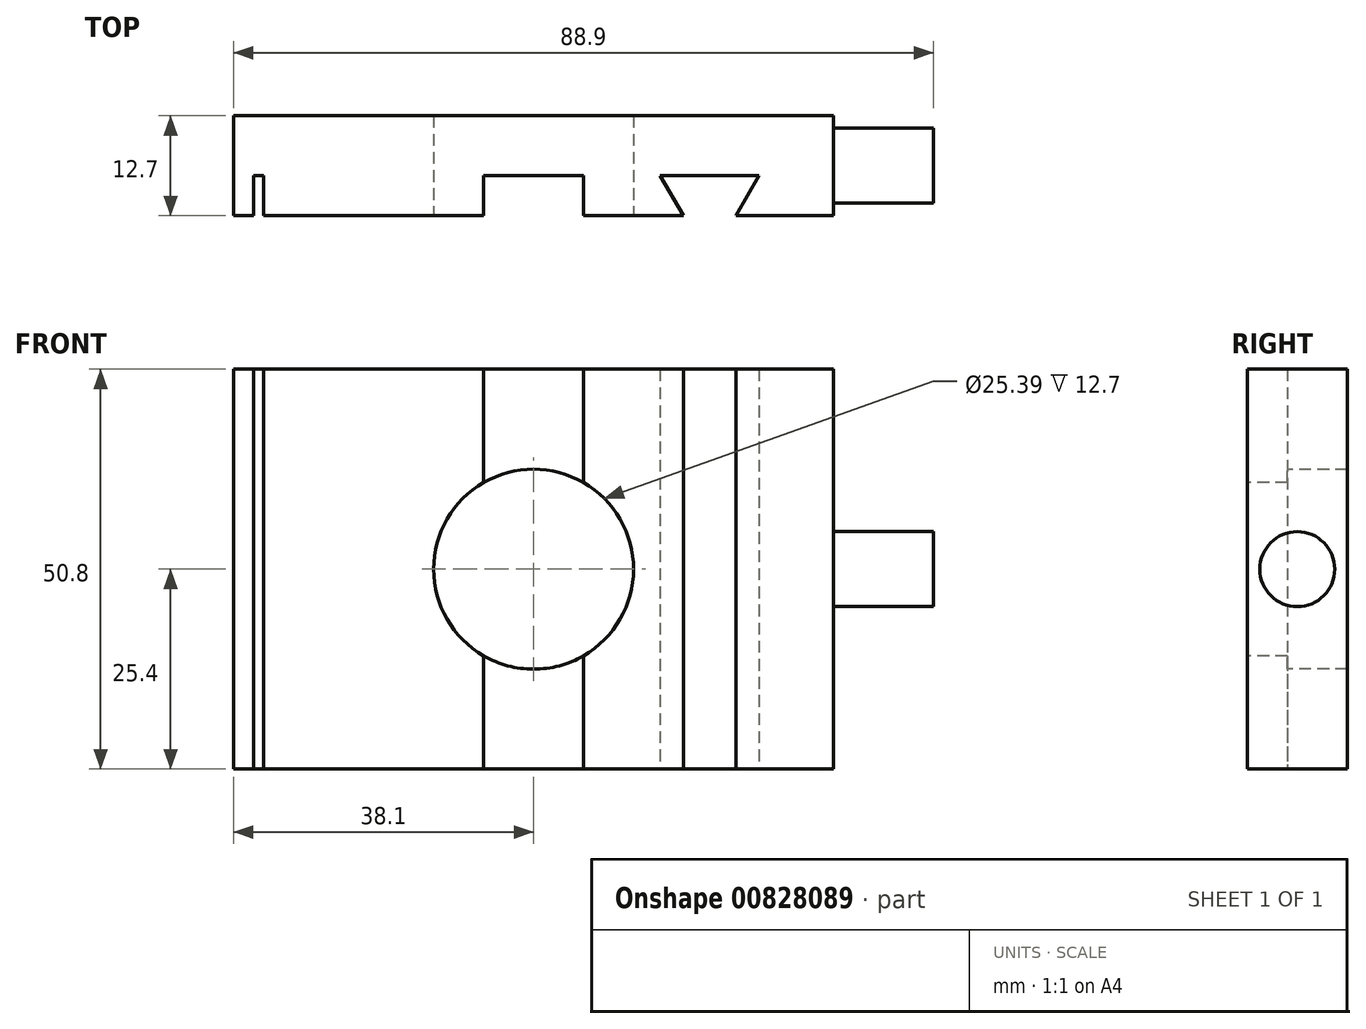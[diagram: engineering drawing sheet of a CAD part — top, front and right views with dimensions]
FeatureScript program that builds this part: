
annotation { "Feature Type Name" : "Feature", "Feature Type Description" : "" }
export const myFeature = defineFeature(function(context is Context, id is Id, definition is map)
    precondition{}
    {
        {
            var Q0;
            Q0=qCreatedBy(makeId("Front.planeOp"),FACE);
            var sketch = newSketch(context, id + "F0", { "sketchPlane" : qUnion([Q0])});
            skLineSegment(sketch, "E0.bottom", {"start": v(38.1, 25.4) * mm, "end": v(-38.1, 25.4) * mm});
            skLineSegment(sketch, "E0.top", {"start": v(38.1, -25.4) * mm, "end": v(-38.1, -25.4) * mm});
            skLineSegment(sketch, "E0.left", {"start": v(38.1, 25.4) * mm, "end": v(38.1, -25.4) * mm});
            skLineSegment(sketch, "E0.right", {"start": v(-38.1, 25.4) * mm, "end": v(-38.1, -25.4) * mm});
            skPoint(sketch, "E0.middle", {"position": v(0, 0) * mm});
            skSolve(sketch);
        }
        {
            var Q0;
            Q0=makeQuery(id+"F0.imprint","IMPRINT",FACE,{"disambiguationData":[TD([[makeQuery(id+"F0.imprint","IMPRINT",EDGE,{"derivedFrom":sQuery(id+"F0.wireOp",EDGE,"E0.bottom")}),1.0]])]});
            extrude(context, id + "F1", {"entities" : qUnion([Q0]), "depth" : 12.7 * mm, "offsetDistance" : 25.4 * mm});
        }
        {
            var Q0;
            Q0=makeQuery(id+"F1.opExtrude","CAP_FACE",FACE,{"disambiguationData":[OSD([sQuery(id+"F0.wireOp",EDGE,"E0.bottom"),sQuery(id+"F0.wireOp",EDGE,"E0.top"),sQuery(id+"F0.wireOp",EDGE,"E0.left"),sQuery(id+"F0.wireOp",EDGE,"E0.right")])],"isStart":false});
            var sketch = newSketch(context, id + "F2", { "sketchPlane" : qUnion([Q0])});
            skLineSegment(sketch, "E1.bottom", {"start": v(-35.56, 25.4) * mm, "end": v(-34.29, 25.4) * mm});
            skLineSegment(sketch, "E1.top", {"start": v(-35.56, -25.4) * mm, "end": v(-34.29, -25.4) * mm});
            skLineSegment(sketch, "E1.left", {"start": v(-35.56, 25.4) * mm, "end": v(-35.56, -25.4) * mm});
            skLineSegment(sketch, "E1.right", {"start": v(-34.29, 25.4) * mm, "end": v(-34.29, -25.4) * mm});
            skCircle(sketch, "E2", {"center": v(0, 0) * mm, "radius": 12.7 * mm});
            skLineSegment(sketch, "E3.bottom", {"start": v(6.35, 25.4) * mm, "end": v(-6.35, 25.4) * mm});
            skLineSegment(sketch, "E3.top", {"start": v(6.35, -25.4) * mm, "end": v(-6.35, -25.4) * mm});
            skLineSegment(sketch, "E3.left", {"start": v(6.35, 25.4) * mm, "end": v(6.35, -25.4) * mm});
            skLineSegment(sketch, "E3.right", {"start": v(-6.35, 25.4) * mm, "end": v(-6.35, -25.4) * mm});
            skSolve(sketch);
        }
        {
            var Q0;
            {var subQ0=sQuery(id+"F2.wireOp",EDGE,"E3.right");var subQ1=sQuery(id+"F2.wireOp",EDGE,"E2");var subQ2=makeQuery(id+"F2.imprint","INTERSECT",VERTEX,{"disambiguationData":[OD(0.0)],"derivedFrom":[subQ1,subQ0]});Q0=makeQuery(id+"F2.imprint","IMPRINT",FACE,{"disambiguationData":[TD([[makeQuery(id+"F2.imprint","IMPRINT",EDGE,{"disambiguationData":[TD([[subQ2,-1.0]])],"derivedFrom":subQ1}),1.0]])]});}
            var Q1;
            {var subQ0=sQuery(id+"F2.wireOp",EDGE,"E3.right");var subQ1=sQuery(id+"F2.wireOp",EDGE,"E2");var subQ2=makeQuery(id+"F2.imprint","INTERSECT",VERTEX,{"disambiguationData":[OD(0.0)],"derivedFrom":[subQ1,subQ0]});Q1=makeQuery(id+"F2.imprint","IMPRINT",FACE,{"disambiguationData":[TD([[makeQuery(id+"F2.imprint","IMPRINT",EDGE,{"disambiguationData":[TD([[subQ2,1.0]])],"derivedFrom":subQ1}),1.0]])]});}
            var Q2;
            {var subQ0=sQuery(id+"F2.wireOp",EDGE,"E3.left");var subQ1=sQuery(id+"F2.wireOp",EDGE,"E2");var subQ2=makeQuery(id+"F2.imprint","INTERSECT",VERTEX,{"disambiguationData":[OD(0.0)],"derivedFrom":[subQ1,subQ0]});Q2=makeQuery(id+"F2.imprint","IMPRINT",FACE,{"disambiguationData":[TD([[makeQuery(id+"F2.imprint","IMPRINT",EDGE,{"disambiguationData":[TD([[subQ2,1.0]])],"derivedFrom":subQ1}),1.0]])]});}
            extrude(context, id + "F3", {"entities" : qUnion([Q0, Q1, Q2]), "operationType" : NewBodyOperationType.REMOVE, "oppositeDirection" : true, "depth" : 12.7 * mm, "offsetDistance" : 25.4 * mm});
        }
        {
            var Q0;
            Q0 = qSketchRegion(id + "F2", true);
            extrude(context, id + "F4", {"entities" : qUnion([Q0]), "operationType" : NewBodyOperationType.REMOVE, "oppositeDirection" : true, "depth" : 5.08 * mm, "offsetDistance" : 25.4 * mm});
        }
        {
            var Q0;
            Q0=makeQuery(id+"F1.opExtrude","SWEPT_FACE",FACE,{"disambiguationData":[OSD([sQuery(id+"F0.wireOp",EDGE,"E0.top")])]});
            var sketch = newSketch(context, id + "F5", { "sketchPlane" : qUnion([Q0])});
            skLineSegment(sketch, "E4", {"start": v(19.02, 12.7) * mm, "end": v(16.09, 7.62) * mm});
            skLineSegment(sketch, "E5", {"start": v(28.64, 7.62) * mm, "end": v(25.7, 12.7) * mm});
            skLineSegment(sketch, "E6", {"start": v(25.7, 12.7) * mm, "end": v(19.02, 12.7) * mm});
            skLineSegment(sketch, "E7", {"start": v(16.09, 7.62) * mm, "end": v(28.64, 7.62) * mm});
            skSolve(sketch);
        }
        {
            var Q0;
            Q0 = qSketchRegion(id + "F5", true);
            extrude(context, id + "F6", {"entities" : qUnion([Q0]), "operationType" : NewBodyOperationType.REMOVE, "oppositeDirection" : true, "depth" : 50.8 * mm, "offsetDistance" : 25.4 * mm});
        }
        {
            var Q0;
            Q0=makeQuery(id+"F1.opExtrude","SWEPT_FACE",FACE,{"disambiguationData":[OSD([sQuery(id+"F0.wireOp",EDGE,"E0.left")])]});
            var sketch = newSketch(context, id + "F7", { "sketchPlane" : qUnion([Q0])});
            skCircle(sketch, "E8", {"center": v(-6.35, 0) * mm, "radius": 4.76 * mm});
            skPoint(sketch, "E8.centerSnap0", {"position": v(-12.7, 0) * mm});
            skPoint(sketch, "E8.centerSnap1", {"position": v(-6.35, -25.4) * mm});
            skSolve(sketch);
        }
        {
            var Q0;
            Q0=makeQuery(id+"F7.imprint","IMPRINT",FACE,{"disambiguationData":[TD([[makeQuery(id+"F7.imprint","IMPRINT",EDGE,{"derivedFrom":sQuery(id+"F7.wireOp",EDGE,"E8")}),1.0]])]});
            extrude(context, id + "F8", {"entities" : qUnion([Q0]), "operationType" : NewBodyOperationType.ADD, "depth" : 12.7 * mm, "offsetDistance" : 25.4 * mm});
        }
    });
